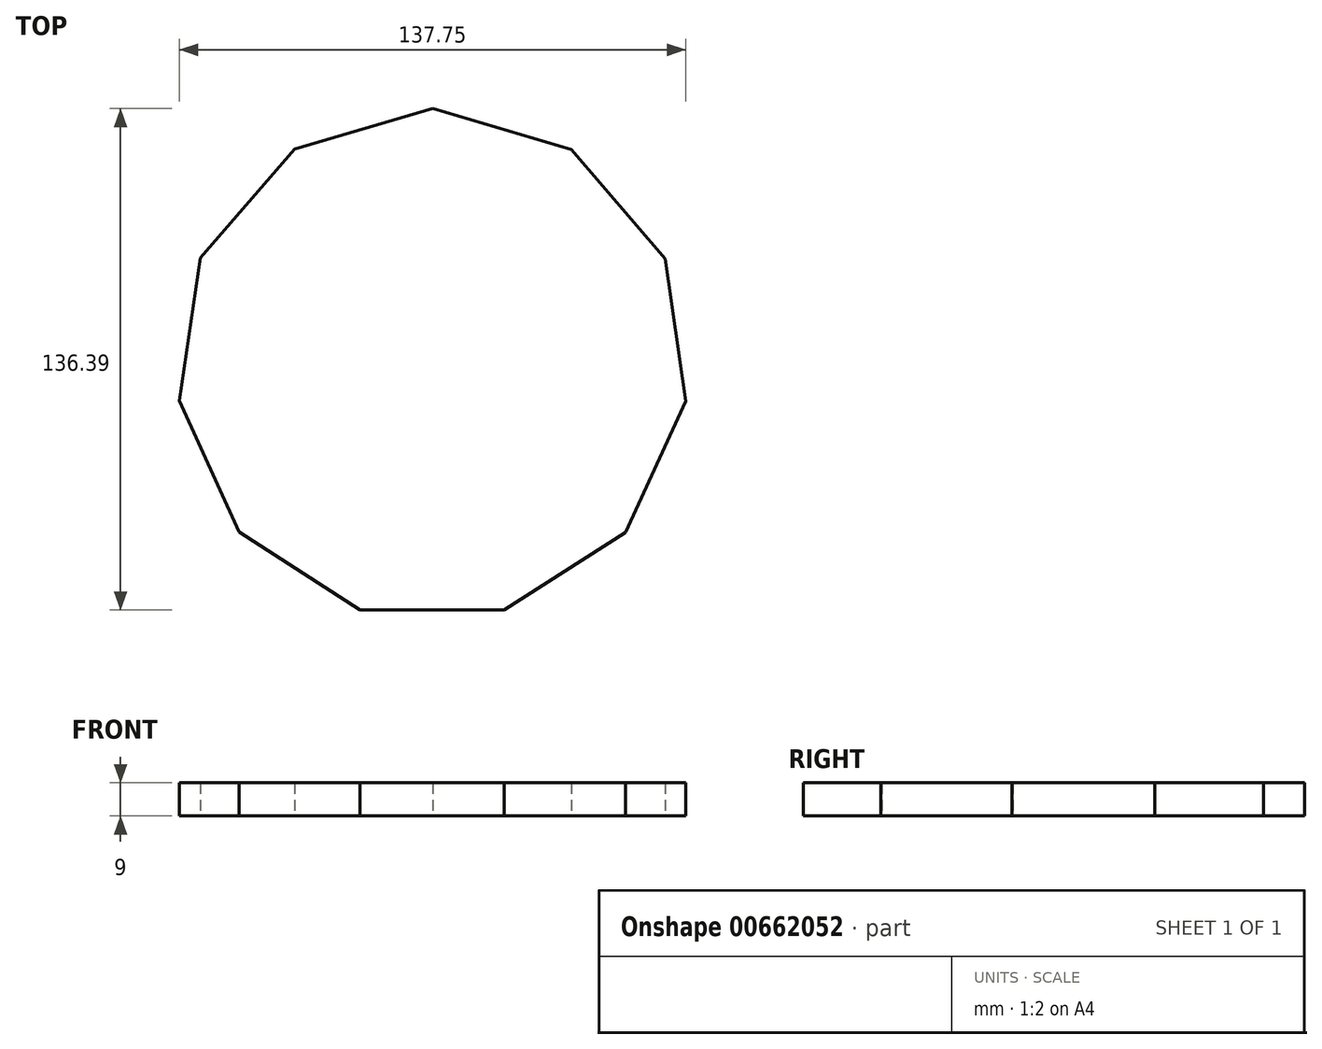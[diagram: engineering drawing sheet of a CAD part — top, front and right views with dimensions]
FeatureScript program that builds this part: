
annotation { "Feature Type Name" : "Feature", "Feature Type Description" : "" }
export const myFeature = defineFeature(function(context is Context, id is Id, definition is map)
    precondition{}
    {
        {
            var Q0;
            Q0=qCreatedBy(makeId("Top.planeOp"),FACE);
            var sketch = newSketch(context, id + "F0", { "sketchPlane" : qUnion([Q0])});
            skCircle(sketch, "E0.cCircle", {"center": v(-4.67, 2.14) * mm, "radius": 66.77 * mm, "construction": true});
            skLineSegment(sketch, "E0.0", {"start": v(64.2, -7.87) * mm, "end": v(47.85, -43.5) * mm});
            skLineSegment(sketch, "E0.1", {"start": v(47.85, -43.5) * mm, "end": v(14.83, -64.66) * mm});
            skLineSegment(sketch, "E0.2", {"start": v(14.83, -64.66) * mm, "end": v(-24.38, -64.6) * mm});
            skLineSegment(sketch, "E0.3", {"start": v(-24.38, -64.6) * mm, "end": v(-57.33, -43.35) * mm});
            skLineSegment(sketch, "E0.4", {"start": v(-57.33, -43.35) * mm, "end": v(-73.56, -7.66) * mm});
            skLineSegment(sketch, "E0.5", {"start": v(-73.56, -7.66) * mm, "end": v(-67.92, 31.14) * mm});
            skLineSegment(sketch, "E0.6", {"start": v(-67.92, 31.14) * mm, "end": v(-42.2, 60.74) * mm});
            skLineSegment(sketch, "E0.7", {"start": v(-42.2, 60.74) * mm, "end": v(-4.56, 71.73) * mm});
            skLineSegment(sketch, "E0.8", {"start": v(-4.56, 71.73) * mm, "end": v(33.04, 60.62) * mm});
            skLineSegment(sketch, "E0.9", {"start": v(33.04, 60.62) * mm, "end": v(58.67, 30.95) * mm});
            skLineSegment(sketch, "E0.10", {"start": v(58.67, 30.95) * mm, "end": v(64.2, -7.87) * mm});
            skPoint(sketch, "E0.0.midPoint", {"position": v(56.02, -25.69) * mm});
            skSolve(sketch);
        }
        {
            var Q0;
            Q0=makeQuery(id+"F0.imprint","IMPRINT",FACE,{"disambiguationData":[TD([[makeQuery(id+"F0.imprint","IMPRINT",EDGE,{"derivedFrom":sQuery(id+"F0.wireOp",EDGE,"E0.0")}),-1.0]])]});
            extrude(context, id + "F1", {"entities" : qUnion([Q0]), "depth" : 9 * mm, "offsetDistance" : 25 * mm});
        }
    });
